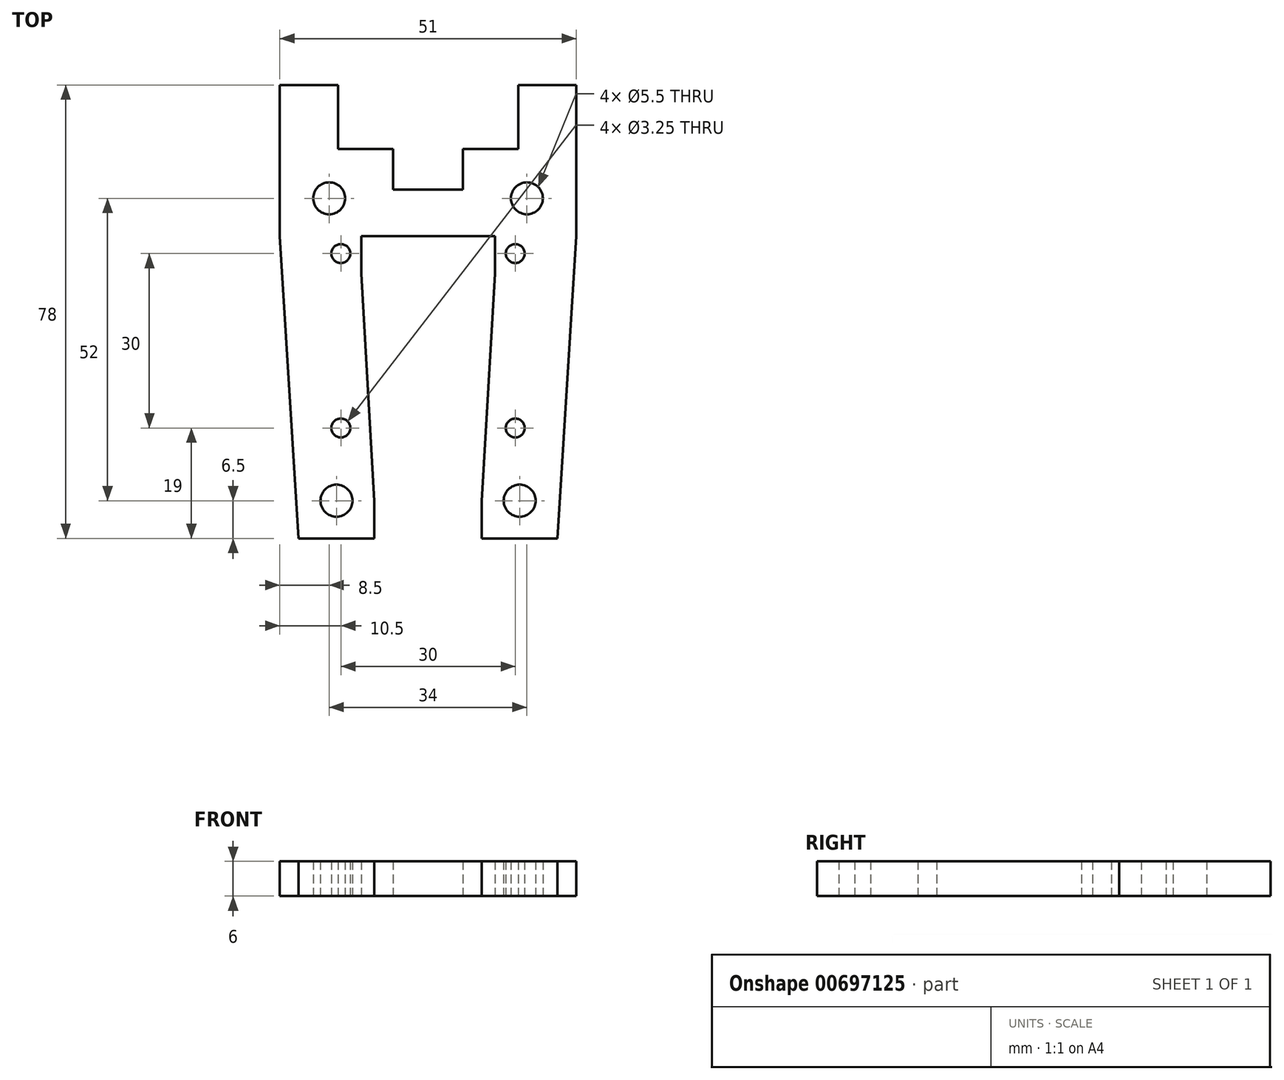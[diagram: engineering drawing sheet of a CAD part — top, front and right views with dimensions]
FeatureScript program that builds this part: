
annotation { "Feature Type Name" : "Feature", "Feature Type Description" : "" }
export const myFeature = defineFeature(function(context is Context, id is Id, definition is map)
    precondition{}
    {
        {
            var Q0;
            Q0=qCreatedBy(makeId("Top.planeOp"),FACE);
            var sketch = newSketch(context, id + "F0", { "sketchPlane" : qUnion([Q0])});
            skCircle(sketch, "E0", {"center": v(-17, 6.5) * mm, "radius": 2.75 * mm});
            skCircle(sketch, "E1", {"center": v(17, 6.5) * mm, "radius": 2.75 * mm});
            skLineSegment(sketch, "E2.top", {"start": v(-15.5, 15) * mm, "end": v(-6, 15) * mm});
            skLineSegment(sketch, "E2.left", {"start": v(-25.5, 0) * mm, "end": v(-25.5, 15) * mm});
            skLineSegment(sketch, "E2.right", {"start": v(25.5, 0) * mm, "end": v(25.5, 15) * mm});
            skLineSegment(sketch, "E3.top", {"start": v(-25.5, 26) * mm, "end": v(-15.5, 26) * mm});
            skLineSegment(sketch, "E3.left", {"start": v(-25.5, 15) * mm, "end": v(-25.5, 26) * mm});
            skLineSegment(sketch, "E3.right", {"start": v(-15.5, 15) * mm, "end": v(-15.5, 26) * mm});
            skLineSegment(sketch, "E4.top", {"start": v(25.5, 26) * mm, "end": v(15.5, 26) * mm});
            skLineSegment(sketch, "E4.left", {"start": v(25.5, 15) * mm, "end": v(25.5, 26) * mm});
            skLineSegment(sketch, "E4.right", {"start": v(15.5, 15) * mm, "end": v(15.5, 26) * mm});
            skLineSegment(sketch, "E5.top", {"start": v(-6, 8) * mm, "end": v(6, 8) * mm});
            skLineSegment(sketch, "E5.left", {"start": v(-6, 15) * mm, "end": v(-6, 8) * mm});
            skLineSegment(sketch, "E5.right", {"start": v(6, 15) * mm, "end": v(6, 8) * mm});
            skLineSegment(sketch, "E6.trimOffspring", {"start": v(6, 15) * mm, "end": v(15.5, 15) * mm});
            skCircle(sketch, "E7", {"center": v(-15.75, -45.5) * mm, "radius": 2.75 * mm});
            skCircle(sketch, "E8", {"center": v(15.75, -45.5) * mm, "radius": 2.75 * mm});
            skCircle(sketch, "E9", {"center": v(-15, -3) * mm, "radius": 1.63 * mm});
            skCircle(sketch, "E10", {"center": v(15, -3) * mm, "radius": 1.63 * mm});
            skCircle(sketch, "E11", {"center": v(-15, -33) * mm, "radius": 1.63 * mm});
            skCircle(sketch, "E12", {"center": v(15, -33) * mm, "radius": 1.63 * mm});
            skLineSegment(sketch, "E13", {"start": v(25.5, 0) * mm, "end": v(22.25, -52) * mm});
            skLineSegment(sketch, "E14", {"start": v(-25.5, 0) * mm, "end": v(-22.25, -52) * mm});
            skLineSegment(sketch, "E15", {"start": v(-11.5, -6.5) * mm, "end": v(-9.25, -45.5) * mm});
            skLineSegment(sketch, "E16", {"start": v(-9.25, -45.5) * mm, "end": v(-9.25, -52) * mm});
            skLineSegment(sketch, "E17", {"start": v(11.5, -6.5) * mm, "end": v(9.25, -45.5) * mm});
            skLineSegment(sketch, "E18", {"start": v(9.25, -45.5) * mm, "end": v(9.25, -52) * mm});
            skLineSegment(sketch, "E19", {"start": v(-11.5, -6.5) * mm, "end": v(-11.5, 0) * mm});
            skLineSegment(sketch, "E20", {"start": v(-11.5, 0) * mm, "end": v(11.5, 0) * mm});
            skLineSegment(sketch, "E21", {"start": v(11.5, 0) * mm, "end": v(11.5, -6.5) * mm});
            skLineSegment(sketch, "E22", {"start": v(-22.25, -52) * mm, "end": v(-9.25, -52) * mm});
            skLineSegment(sketch, "E23", {"start": v(9.25, -52) * mm, "end": v(22.25, -52) * mm});
            skSolve(sketch);
        }
        {
            var Q0;
            Q0=makeQuery(id+"F0.imprint","IMPRINT",FACE,{"disambiguationData":[TD([[makeQuery(id+"F0.imprint","IMPRINT",EDGE,{"derivedFrom":sQuery(id+"F0.wireOp",EDGE,"E0")}),-1.0]])]});
            extrude(context, id + "F1", {"entities" : qUnion([Q0]), "depth" : 6 * mm, "offsetDistance" : 25 * mm});
        }
    });
